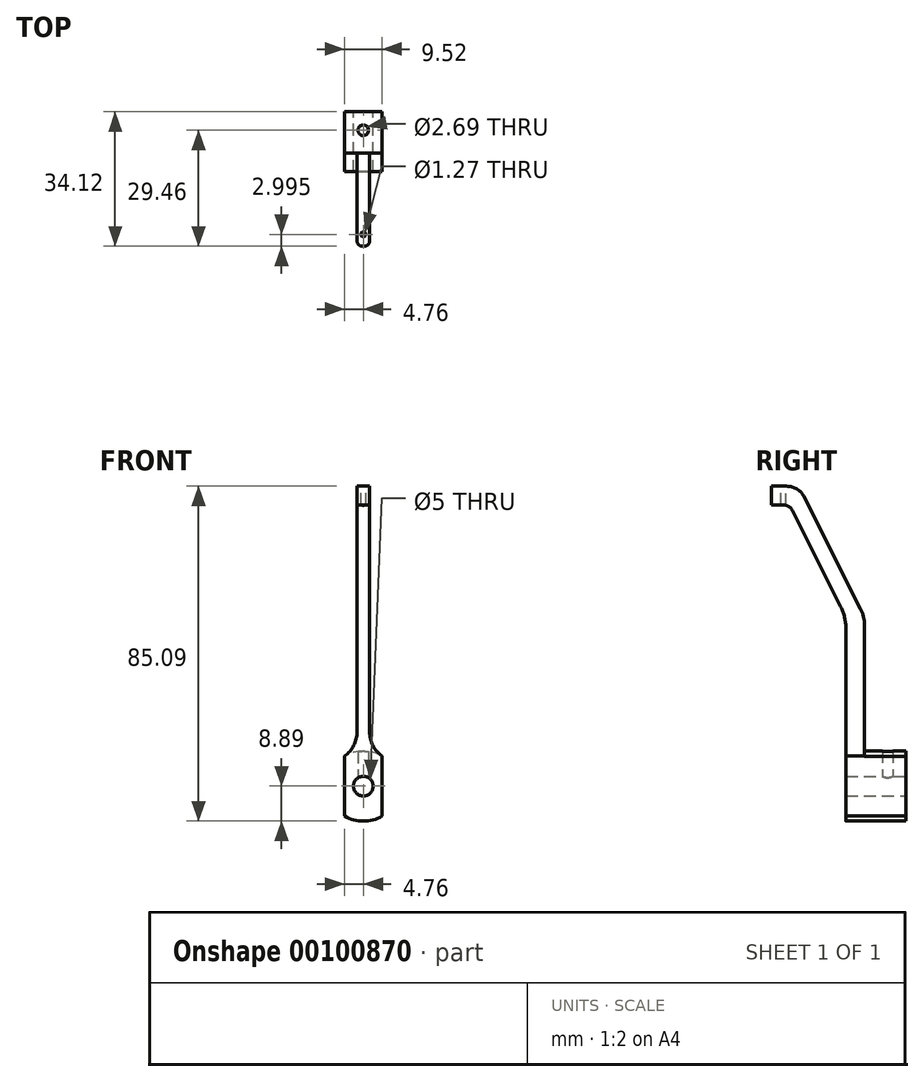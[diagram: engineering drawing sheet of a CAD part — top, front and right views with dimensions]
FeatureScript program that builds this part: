
annotation { "Feature Type Name" : "Feature", "Feature Type Description" : "" }
export const myFeature = defineFeature(function(context is Context, id is Id, definition is map)
    precondition{}
    {
        {
            var Q0;
            Q0=qCreatedBy(makeId("Front.planeOp"),FACE);
            var sketch = newSketch(context, id + "F0", { "sketchPlane" : qUnion([Q0])});
            skCircle(sketch, "E0", {"center": v(0, 0) * mm, "radius": 2.24 * mm});
            skLineSegment(sketch, "E1", {"start": v(-8.89, 12.93) * mm, "end": v(-3.17, 76.2) * mm});
            skLineSegment(sketch, "E2", {"start": v(-3.18, 76.2) * mm, "end": v(3.18, 76.2) * mm});
            skLineSegment(sketch, "E3", {"start": v(3.17, 76.2) * mm, "end": v(8.9, 12.93) * mm});
            skLineSegment(sketch, "E4", {"start": v(8.9, 12.93) * mm, "end": v(8.9, -12.47) * mm});
            skLineSegment(sketch, "E5", {"start": v(-8.89, -12.47) * mm, "end": v(-8.89, 12.93) * mm});
            skLineSegment(sketch, "E6", {"start": v(0, 76.2) * mm, "end": v(0, 0) * mm, "construction": true});
            skLineSegment(sketch, "E7", {"start": v(-6.35, 12.81) * mm, "end": v(-1.2, 69.85) * mm});
            skLineSegment(sketch, "E8", {"start": v(-1.2, 69.85) * mm, "end": v(1.2, 69.85) * mm});
            skLineSegment(sketch, "E9.trimOffspring", {"start": v(1.2, 69.85) * mm, "end": v(6.35, 12.81) * mm});
            skArc(sketch, "E10", {"start": v(6.35, 0) * mm, "mid": v(0, 6.35) * mm, "end": v(-6.35, 0) * mm});
            skLineSegment(sketch, "E11", {"start": v(-6.35, 12.81) * mm, "end": v(-6.35, 0) * mm});
            skLineSegment(sketch, "E12", {"start": v(6.35, 12.81) * mm, "end": v(6.35, 0) * mm});
            skArc(sketch, "E13.trimOffspring", {"start": v(-8.89, -12.47) * mm, "mid": v(0, -21.36) * mm, "end": v(8.9, -12.47) * mm});
            skSolve(sketch);
        }
        {
            var Q0;
            Q0=qCreatedBy(makeId("Right.planeOp"),FACE);
            var sketch = newSketch(context, id + "F1", { "sketchPlane" : qUnion([Q0])});
            skLineSegment(sketch, "E14", {"start": v(-18.88, 71.44) * mm, "end": v(-15.88, 71.44) * mm});
            skLineSegment(sketch, "E15", {"start": v(-13.6, 70.04) * mm, "end": v(-1.36, 45.66) * mm});
            skLineSegment(sketch, "E16", {"start": v(0, 39.94) * mm, "end": v(0, -8.89) * mm});
            skLineSegment(sketch, "E17", {"start": v(0, -8.89) * mm, "end": v(15.24, -8.89) * mm});
            skLineSegment(sketch, "E18", {"start": v(15.24, -8.89) * mm, "end": v(15.24, 8.89) * mm});
            skLineSegment(sketch, "E19", {"start": v(15.24, 8.9) * mm, "end": v(4.76, 8.89) * mm});
            skLineSegment(sketch, "E20", {"start": v(4.76, 8.89) * mm, "end": v(4.76, 40.63) * mm});
            skLineSegment(sketch, "E21", {"start": v(3.72, 45.04) * mm, "end": v(-10.53, 73.4) * mm});
            skLineSegment(sketch, "E22", {"start": v(15.24, 0) * mm, "end": v(0, 0) * mm, "construction": true});
            skPoint(sketch, "E23.visualSharp", {"position": v(0, 42.96) * mm});
            skArc(sketch, "E23.filletArc", {"start": v(0, 39.94) * mm, "mid": v(-0.34, 42.88) * mm, "end": v(-1.36, 45.66) * mm});
            skPoint(sketch, "E24.visualSharp", {"position": v(4.76, 42.96) * mm});
            skArc(sketch, "E24.filletArc", {"start": v(4.76, 40.63) * mm, "mid": v(4.5, 42.9) * mm, "end": v(3.72, 45.04) * mm});
            skPoint(sketch, "E25.visualSharp", {"position": v(-34.08, 120.27) * mm});
            skArc(sketch, "E25.filletArc", {"start": v(-10.53, 73.4) * mm, "mid": v(-12.4, 75.44) * mm, "end": v(-15.07, 76.2) * mm});
            skLineSegment(sketch, "E26", {"start": v(4.76, 8.89) * mm, "end": v(0, 8.89) * mm});
            skLineSegment(sketch, "E27", {"start": v(-15.07, 76.2) * mm, "end": v(-18.88, 76.2) * mm});
            skLineSegment(sketch, "E28", {"start": v(-18.88, 76.2) * mm, "end": v(-18.88, 71.44) * mm});
            skPoint(sketch, "E29.visualSharp", {"position": v(-14.3, 71.44) * mm});
            skArc(sketch, "E29.filletArc", {"start": v(-13.6, 70.04) * mm, "mid": v(-14.54, 71.06) * mm, "end": v(-15.88, 71.44) * mm});
            skLineSegment(sketch, "E30", {"start": v(-15.88, 128.59) * mm, "end": v(-15.88, 114.65) * mm, "construction": true});
            skSolve(sketch);
        }
        {
            var Q0;
            Q0=makeQuery(id+"F1.imprint","IMPRINT",FACE,{"disambiguationData":[TD([[makeQuery(id+"F1.imprint","IMPRINT",EDGE,{"derivedFrom":sQuery(id+"F1.wireOp",EDGE,"E14")}),1.0]])]});
            extrude(context, id + "F2", {"entities" : qUnion([Q0]), "depth" : 1.59 * mm, "hasSecondDirection" : true, "secondDirectionOppositeDirection" : true, "secondDirectionDepth" : 1.59 * mm});
        }
        {
            var Q0;
            {var subQ1=sQuery(id+"F1.wireOp",EDGE,"fNuClo9G-gxgB-ZKoF-5ek1-GzOPS4ueQ6zA");Q0=makeQuery(id+"F1.imprint","IMPRINT",FACE,{"disambiguationData":[TD([[makeQuery(id+"F1.imprint","IMPRINT",EDGE,{"derivedFrom":subQ1}),-1.0]])]});}
            var Q1;
            {var subQ0=sQuery(id+"F1.wireOp",EDGE,"E17");Q1=makeQuery(id+"F1.imprint","IMPRINT",FACE,{"disambiguationData":[TD([[makeQuery(id+"F1.imprint","IMPRINT",EDGE,{"derivedFrom":subQ0}),1.0]])]});}
            extrude(context, id + "F3", {"entities" : qUnion([Q0, Q1]), "operationType" : NewBodyOperationType.ADD, "depth" : 9.52 * mm, "hasSecondDirection" : true, "secondDirectionOppositeDirection" : true, "secondDirectionDepth" : 9.52 * mm});
        }
        {
            var Q0;
            Q0=makeQuery(id+"F3.opExtrude","CAP_EDGE",EDGE,{"disambiguationData":[OSD([sQuery(id+"F1.wireOp",EDGE,"E19"),sQuery(id+"F1.wireOp",EDGE,"E26")])],"isStart":false});
            var Q1;
            Q1=makeQuery(id+"F3.opExtrude","CAP_EDGE",EDGE,{"disambiguationData":[OSD([sQuery(id+"F1.wireOp",EDGE,"E17")])],"isStart":false});
            var Q2;
            Q2=makeQuery(id+"F3.opExtrude","CAP_EDGE",EDGE,{"disambiguationData":[OSD([sQuery(id+"F1.wireOp",EDGE,"XDOwbMyA-zM0q-oljK-1kD4-75xqVUQpscfp"),sQuery(id+"F1.wireOp",EDGE,"LLpKUasx-zCht-fIpE-OXn2-U5VEhtcayuCd")])],"isStart":false});
            var Q3;
            Q3=makeQuery(id+"F3.opExtrude","CAP_EDGE",EDGE,{"disambiguationData":[OSD([sQuery(id+"F1.wireOp",EDGE,"fNuClo9G-gxgB-ZKoF-5ek1-GzOPS4ueQ6zA")])],"isStart":false});
            var Q4;
            Q4=makeQuery(id+"F3.opExtrude","CAP_EDGE",EDGE,{"disambiguationData":[OSD([sQuery(id+"F1.wireOp",EDGE,"E19"),sQuery(id+"F1.wireOp",EDGE,"E26")])],"isStart":true});
            var Q5;
            Q5=makeQuery(id+"F3.opExtrude","CAP_EDGE",EDGE,{"disambiguationData":[OSD([sQuery(id+"F1.wireOp",EDGE,"XDOwbMyA-zM0q-oljK-1kD4-75xqVUQpscfp"),sQuery(id+"F1.wireOp",EDGE,"LLpKUasx-zCht-fIpE-OXn2-U5VEhtcayuCd")])],"isStart":true});
            var Q6;
            Q6=makeQuery(id+"F3.opExtrude","CAP_EDGE",EDGE,{"disambiguationData":[OSD([sQuery(id+"F1.wireOp",EDGE,"fNuClo9G-gxgB-ZKoF-5ek1-GzOPS4ueQ6zA")])],"isStart":true});
            var Q7;
            Q7=makeQuery(id+"F3.opExtrude","CAP_EDGE",EDGE,{"disambiguationData":[OSD([sQuery(id+"F1.wireOp",EDGE,"E17")])],"isStart":true});
            fillet(context, id + "F4", {"entities" : qUnion([Q0, Q1, Q2, Q3, Q4, Q5, Q6, Q7]), "radius" : 9.52 * mm, "tangentPropagation" : true, "allowEdgeOverflow" : false});
        }
        {
            var Q0;
            Q0=makeQuery(id+"F3.opExtrude","SWEPT_FACE",FACE,{"disambiguationData":[OSD([sQuery(id+"F1.wireOp",EDGE,"E18")])]});
            var sketch = newSketch(context, id + "F5", { "sketchPlane" : qUnion([Q0])});
            skCircle(sketch, "E31", {"center": v(0, 0) * mm, "radius": 2.5 * mm});
            skSolve(sketch);
        }
        {
            var Q0;
            Q0 = qSketchRegion(id + "F5", true);
            extrude(context, id + "F6", {"entities" : qUnion([Q0]), "operationType" : NewBodyOperationType.REMOVE, "endBound" : BoundingType.THROUGH_ALL, "oppositeDirection" : true, "depth" : 25.4 * mm});
        }
        {
            var Q0;
            Q0=qCreatedBy(makeId("Top.planeOp"),FACE);
            var sketch = newSketch(context, id + "F7", { "sketchPlane" : qUnion([Q0])});
            skLineSegment(sketch, "E32", {"start": v(0, 21.16) * mm, "end": v(0, 0) * mm, "construction": true});
            skCircle(sketch, "E33", {"center": v(0, 10.58) * mm, "radius": 1.35 * mm});
            skLineSegment(sketch, "E34", {"start": v(0, -31.72) * mm, "end": v(0, -22.22) * mm, "construction": true});
            skCircle(sketch, "E35", {"center": v(0, -26.97) * mm, "radius": 1.35 * mm});
            skCircle(sketch, "E36", {"center": v(0, 10.58) * mm, "radius": 3.81 * mm, "construction": true});
            skSolve(sketch);
        }
        {
            var Q0;
            Q0 = qSketchRegion(id + "F7", true);
            var Q1;
            Q1=sQuery(id+"F7.wireOp",EDGE,"E33");
            var Q2;
            Q2=sQuery(id+"F7.wireOp",EDGE,"E35");
            extrude(context, id + "F8", {"entities" : qUnion([Q0]), "operationType" : NewBodyOperationType.REMOVE, "surfaceEntities" : qUnion([Q1, Q2]), "depth" : 25.4 * mm});
        }
        {
            var Q0;
            Q0=makeQuery(id+"F4.opFillet","BLEND_EDGE",EDGE,{"blendedFrom":[makeQuery(id+"F3.opExtrude","CAP_EDGE",EDGE,{"disambiguationData":[OSD([sQuery(id+"F1.wireOp",EDGE,"E17")])],"isStart":true}),makeQuery(id+"F3.opExtrude","CAP_EDGE",EDGE,{"disambiguationData":[OSD([sQuery(id+"F1.wireOp",EDGE,"E19"),sQuery(id+"F1.wireOp",EDGE,"E26")])],"isStart":true})],"blendedInto":[]});
            var Q1;
            {var subQ0=sQuery(id+"F1.wireOp",EDGE,"E26");Q1=makeQuery(id+"F4.opFillet","BLEND_EDGE",EDGE,{"blendedFrom":[makeQuery(id+"F3.opExtrude","CAP_EDGE",EDGE,{"disambiguationData":[OSD([sQuery(id+"F1.wireOp",EDGE,"E19"),subQ0])],"isStart":true}),makeQuery(id+"F2.opExtrude","CAP_FACE",FACE,{"disambiguationData":[OSD([sQuery(id+"F1.wireOp",EDGE,"E14"),sQuery(id+"F1.wireOp",EDGE,"E15"),sQuery(id+"F1.wireOp",EDGE,"E16"),sQuery(id+"F1.wireOp",EDGE,"E20"),sQuery(id+"F1.wireOp",EDGE,"E21"),sQuery(id+"F1.wireOp",EDGE,"E23.filletArc"),sQuery(id+"F1.wireOp",EDGE,"E24.filletArc"),sQuery(id+"F1.wireOp",EDGE,"E25.filletArc"),subQ0,sQuery(id+"F1.wireOp",EDGE,"E27"),sQuery(id+"F1.wireOp",EDGE,"E28"),sQuery(id+"F1.wireOp",EDGE,"E29.filletArc")])],"isStart":true})],"blendedInto":[makeQuery(id+"F2.opExtrude","CAP_FACE",FACE,{"disambiguationData":[OSD([sQuery(id+"F1.wireOp",EDGE,"E14"),sQuery(id+"F1.wireOp",EDGE,"E15"),sQuery(id+"F1.wireOp",EDGE,"E16"),sQuery(id+"F1.wireOp",EDGE,"E20"),sQuery(id+"F1.wireOp",EDGE,"E21"),sQuery(id+"F1.wireOp",EDGE,"E23.filletArc"),sQuery(id+"F1.wireOp",EDGE,"E24.filletArc"),sQuery(id+"F1.wireOp",EDGE,"E25.filletArc"),subQ0,sQuery(id+"F1.wireOp",EDGE,"E27"),sQuery(id+"F1.wireOp",EDGE,"E28"),sQuery(id+"F1.wireOp",EDGE,"E29.filletArc")])],"isStart":true})]});}
            var Q2;
            {var subQ0=sQuery(id+"F1.wireOp",EDGE,"E26");Q2=makeQuery(id+"F4.opFillet","BLEND_EDGE",EDGE,{"blendedFrom":[makeQuery(id+"F3.opExtrude","CAP_EDGE",EDGE,{"disambiguationData":[OSD([sQuery(id+"F1.wireOp",EDGE,"E19"),subQ0])],"isStart":false}),makeQuery(id+"F2.opExtrude","CAP_FACE",FACE,{"disambiguationData":[OSD([sQuery(id+"F1.wireOp",EDGE,"E14"),sQuery(id+"F1.wireOp",EDGE,"E15"),sQuery(id+"F1.wireOp",EDGE,"E16"),sQuery(id+"F1.wireOp",EDGE,"E20"),sQuery(id+"F1.wireOp",EDGE,"E21"),sQuery(id+"F1.wireOp",EDGE,"E23.filletArc"),sQuery(id+"F1.wireOp",EDGE,"E24.filletArc"),sQuery(id+"F1.wireOp",EDGE,"E25.filletArc"),subQ0,sQuery(id+"F1.wireOp",EDGE,"E27"),sQuery(id+"F1.wireOp",EDGE,"E28"),sQuery(id+"F1.wireOp",EDGE,"E29.filletArc")])],"isStart":false})],"blendedInto":[makeQuery(id+"F2.opExtrude","CAP_FACE",FACE,{"disambiguationData":[OSD([sQuery(id+"F1.wireOp",EDGE,"E14"),sQuery(id+"F1.wireOp",EDGE,"E15"),sQuery(id+"F1.wireOp",EDGE,"E16"),sQuery(id+"F1.wireOp",EDGE,"E20"),sQuery(id+"F1.wireOp",EDGE,"E21"),sQuery(id+"F1.wireOp",EDGE,"E23.filletArc"),sQuery(id+"F1.wireOp",EDGE,"E24.filletArc"),sQuery(id+"F1.wireOp",EDGE,"E25.filletArc"),subQ0,sQuery(id+"F1.wireOp",EDGE,"E27"),sQuery(id+"F1.wireOp",EDGE,"E28"),sQuery(id+"F1.wireOp",EDGE,"E29.filletArc")])],"isStart":false})]});}
            fillet(context, id + "F9", {"entities" : qUnion([Q0, Q1, Q2]), "radius" : 7.62 * mm, "tangentPropagation" : true, "allowEdgeOverflow" : false});
        }
        {
            var Q0;
            Q0=makeQuery(id+"F2.opExtrude","SWEPT_FACE",FACE,{"disambiguationData":[OSD([sQuery(id+"F1.wireOp",EDGE,"E27")])]});
            var sketch = newSketch(context, id + "F10", { "sketchPlane" : qUnion([Q0])});
            skCircle(sketch, "E37", {"center": v(0, -15.88) * mm, "radius": 0.64 * mm});
            skSolve(sketch);
        }
        {
            var Q0;
            Q0 = qSketchRegion(id + "F10", true);
            extrude(context, id + "F11", {"entities" : qUnion([Q0]), "operationType" : NewBodyOperationType.REMOVE, "oppositeDirection" : true, "depth" : 25.4 * mm});
        }
        {
            var Q0;
            Q0=makeQuery(id+"F2.opExtrude","CAP_EDGE",EDGE,{"disambiguationData":[OSD([sQuery(id+"F1.wireOp",EDGE,"E28")])],"isStart":false});
            var Q1;
            Q1=makeQuery(id+"F2.opExtrude","CAP_EDGE",EDGE,{"disambiguationData":[OSD([sQuery(id+"F1.wireOp",EDGE,"E28")])],"isStart":true});
            fillet(context, id + "F12", {"entities" : qUnion([Q0, Q1]), "radius" : 1.27 * mm, "tangentPropagation" : true, "allowEdgeOverflow" : false});
        }
        {
            var Q0;
            Q0=makeQuery(id+"F5.imprint","IMPRINT",FACE,{"disambiguationData":[TD([[makeQuery(id+"F5.imprint","IMPRINT",EDGE,{"derivedFrom":sQuery(id+"F5.wireOp",EDGE,"E31")}),-1.0]])]});
            var sketch = newSketch(context, id + "F13", { "sketchPlane" : qUnion([Q0])});
            skLineSegment(sketch, "E38", {"start": v(-4.76, 10.8) * mm, "end": v(-4.76, -11.64) * mm});
            skLineSegment(sketch, "E39", {"start": v(-4.76, -11.64) * mm, "end": v(4.76, -11.64) * mm});
            skLineSegment(sketch, "E40", {"start": v(4.76, -11.64) * mm, "end": v(4.76, 10.8) * mm});
            skLineSegment(sketch, "E41", {"start": v(4.76, 10.8) * mm, "end": v(11.74, 10.8) * mm});
            skLineSegment(sketch, "E42", {"start": v(11.74, 10.8) * mm, "end": v(11.74, -15.54) * mm});
            skLineSegment(sketch, "E43", {"start": v(11.74, -15.54) * mm, "end": v(-9.69, -15.54) * mm});
            skLineSegment(sketch, "E44", {"start": v(-9.69, -15.54) * mm, "end": v(-9.69, 10.8) * mm});
            skLineSegment(sketch, "E45", {"start": v(-9.69, 10.8) * mm, "end": v(-4.76, 10.8) * mm});
            skLineSegment(sketch, "E46", {"start": v(0, 0) * mm, "end": v(0, -11.64) * mm, "construction": true});
            skSolve(sketch);
        }
        {
            var Q0;
            Q0 = qSketchRegion(id + "F13", true);
            extrude(context, id + "F14", {"entities" : qUnion([Q0]), "operationType" : NewBodyOperationType.REMOVE, "endBound" : BoundingType.THROUGH_ALL, "oppositeDirection" : true, "depth" : 25.4 * mm});
        }
    });
